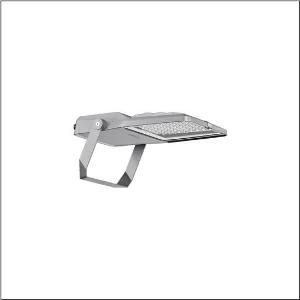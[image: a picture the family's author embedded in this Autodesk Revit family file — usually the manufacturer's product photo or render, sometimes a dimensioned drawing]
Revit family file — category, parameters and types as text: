
# Revit family: floodlight_fl_21_iq_mini___pl33t_5xa7772d5f1a_ae39
name_source: partatom
category: Lighting Fixtures
units: mm (PartAtom-declared; Revit-internal decimal feet)

## family parameters
Cut with Voids When Loaded = No
Host = Face
Light Source = No
Part Type = Normal
Room Calculation Point = No
Round Connector Dimension = Use Diameter
Shared = No

## types (1)
- --- (1 x LED, 16450 lm, 143 W, 4000K)
    Apparent Load = 143 VA
    CIE Flux Codes = 26 75 99 100 100
    Color Rendering = 80
    Color Temperature = 4000K
    Default Elevation = 1800 mm
    Description = Floodlight FL 21 iQ mini, floodlight, primary light control with lens, of PMMA, primary optical cover: protective disc, of toughened safety glass, transparent, light distribution: PL33T, light emission: direct distribution, installation type: surface-mounted, lamps: LED, High Power LED, rated values: 16.450lm | 143W | 115lm/W (begin service life); end service life: 16.450lm | 151,6W; at 50% lumin. flux: 8.225lm | 60,6W | 135,7lm/W, colour temperature: 4000K, colour rendering: CRI > 80, light colour: 840, light setting 1 begin service life: 100% | 16.450lm | 143W | 115lm/W | 4.000K, light setting 1 end service life: 151,6W, further light settings possible, control: Street-Remote, Auto-Match, Temp-Guard, Night-Set, Smart-Wire, Desk-Remote (wireless, voltage-free reading and setting of iQ features in the workshop via application-optimized NFC function/RFID function), optimised constant luminous flux control (CLO 2.0), pre-setting: linear dimming characteristic, with terminal, 6-pole, mains connection: 220..240V, AC, 50/60Hz, luminaire housing, of diecast aluminium, powder-coated, SITECO metallic grey (DB 702S), corrosivity category C5 mid according to DIN EN ISO 12944suitable for swimming poolschlorine-resistant, sealing non-destructively replaceable, mounting bracket, of steel, galvanised, powder-coated, SITECO metallic grey (DB 702S), protection rating (complete): IP66, insulation class (complete): insulation class II (safety insulation), certification: CE, ENEC, VDE, protection symbol: D, impact resistance: IK08, permissible operating ambient temperature: -40..+40°C, permissible operating ambient temperature for outdoor applications: -40..+50°C, standard: DIN EN 12944, LABS conformity tested according to VDMA 24364:2018-05, packaging unit: 1 piece

Light Distribution: PL33T
    Height = 70 mm
    Lamp = 1 x LED
    Lamp Light Flux = 16450 lm
    Lamp Power = 143 W
    Lamp count = 1
    Length = 485 mm
    Luminous efficacy = 115 lm/W
    Manufacturer = Siteco
    ModVariant = No
    Model = 5XA7772D5F1A
    Mounting Place = Pole
    Mounting Type = Pole annexe
    Number of Poles = 1
    OnlyDefault = Yes
    Power Factor = 1
    Product Name = Floodlight FL 21 iQ mini | PL33T
    Product group = floodlight | pylon annexe
    ProductGroupID = 6201
    Protection Class = Protection class II
    Protection Degree = IP 66
    RLX_Detail_Level = 1
    RLX_Emergency_Light_Flux = 0 lm
    RLX_Emergency_Type = 0
    RLX_Emergency_Type_DB = No
    RlxData = <blob elided: 96605 chars, md5=57e734bf>
    Socket = socket
    Standby Power = 0 W
    System Light Flux = 16450 lm
    System Power = 143 W
    Type Comments = factory setting: luminous flux: 100 % | dim-lin: 254 | 730 mA
    Type Image = l_1006845.jpg
    URL = http://relux.com
    VarID = @adj_149793
    Voltage = 0 V
    Weight = 0.00 kg
    Width = 337 mm

## geometry (parser evidence)
native form markers: Blend x4, Sweep x13
no freeform markers — native parametric forms only
